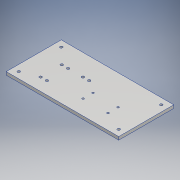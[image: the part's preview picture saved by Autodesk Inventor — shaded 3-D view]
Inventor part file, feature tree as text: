
AUTODESK INVENTOR PART (.ipt)
format: ipt  version: 2017 (Build 210142000, 142)  size: 156,160 bytes
history: native  units: mm
features: sketch x5, hole x4, extrude x1
ambient origin geometry x8: Origin, YZ Plane, XZ Plane, XY Plane, X Axis, Y Axis, Z Axis, Center Point
bodies: Solide1 (feature_tree)
feature tree (10):
  extrude  "Extrusion1"  Depth=180.0mm
  hole  "Perçage_moteur"  [1 undecoded]
  hole  "Perçage_laser"  [1 undecoded]
  hole  "Perçage_coins"  [1 undecoded]
  hole  "Perçage4"  [1 undecoded]
  sketch  "Esquisse1"
  sketch  "Esquisse2"
  sketch  "Esquisse3"
  sketch  "Esquisse4"
  sketch  "Esquisse5"
note: 4 required parameter values undecoded (feature->parameter linkage not recoverable at this tier; creation-order binding heuristic only, values carry confidence <= 0.55)
